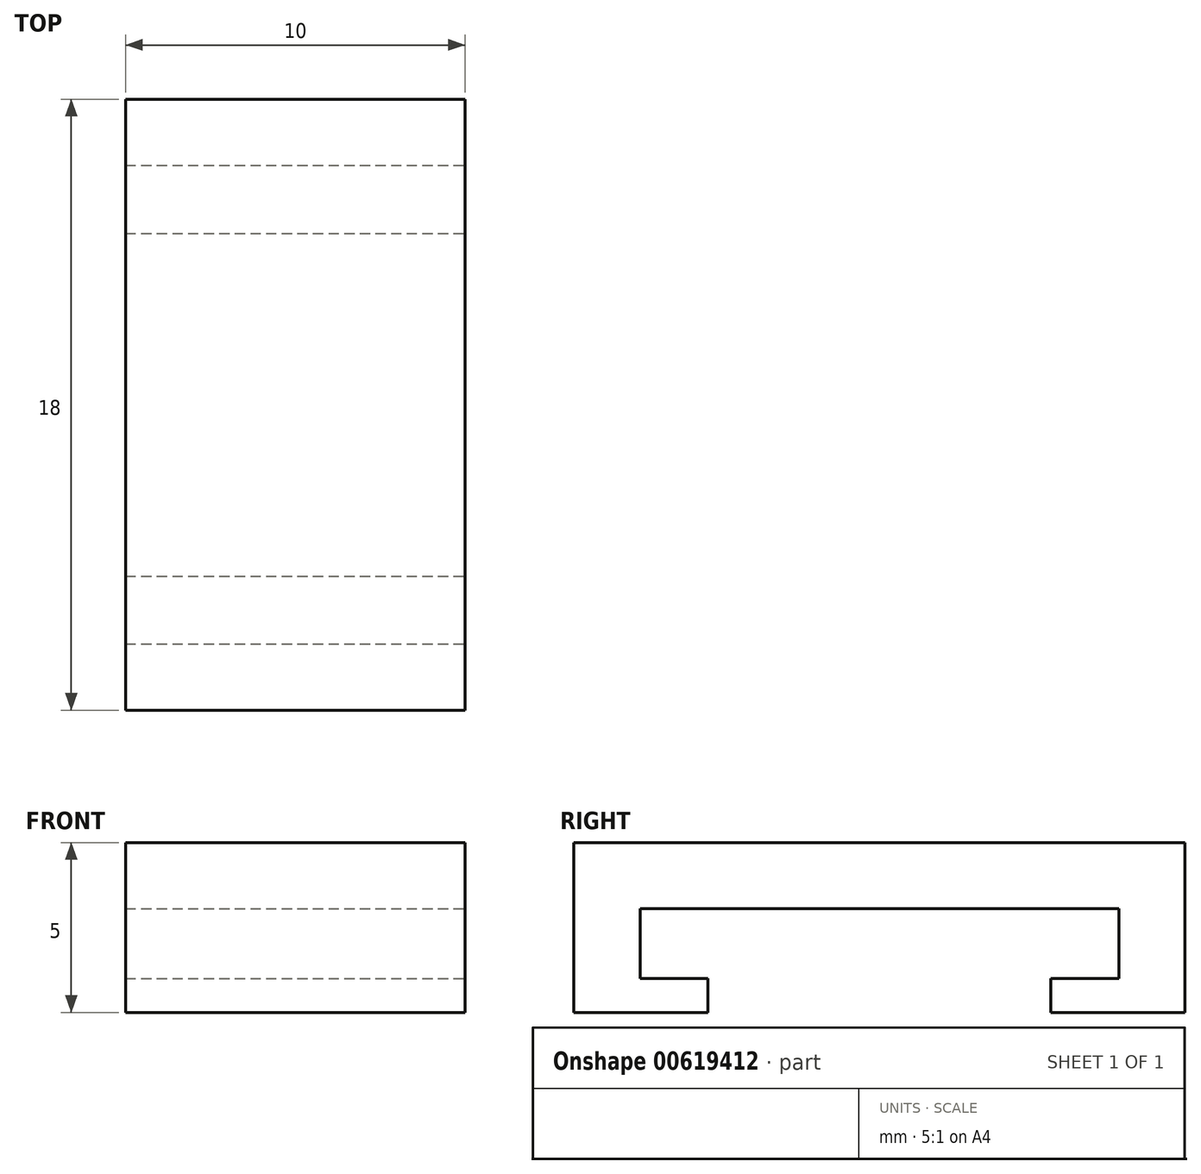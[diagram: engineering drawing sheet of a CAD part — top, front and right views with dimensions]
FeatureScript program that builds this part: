
annotation { "Feature Type Name" : "Feature", "Feature Type Description" : "" }
export const myFeature = defineFeature(function(context is Context, id is Id, definition is map)
    precondition{}
    {
        {
            var Q0;
            Q0=qCreatedBy(makeId("Top.planeOp"),FACE);
            var sketch = newSketch(context, id + "F0", { "sketchPlane" : qUnion([Q0])});
            skLineSegment(sketch, "E0.bottom", {"start": v(-5, 9) * mm, "end": v(5, 9) * mm});
            skLineSegment(sketch, "E0.top", {"start": v(-5, -9) * mm, "end": v(5, -9) * mm});
            skLineSegment(sketch, "E0.left", {"start": v(-5, 9) * mm, "end": v(-5, -9) * mm});
            skLineSegment(sketch, "E0.right", {"start": v(5, 9) * mm, "end": v(5, -9) * mm});
            skPoint(sketch, "E0.middle", {"position": v(0, 0) * mm});
            skSolve(sketch);
        }
        {
            var Q0;
            Q0 = qSketchRegion(id + "F0", true);
            extrude(context, id + "F1", {"entities" : qUnion([Q0]), "depth" : 5 * mm, "offsetDistance" : 25 * mm});
        }
        {
            var Q0;
            Q0=makeQuery(id+"F1.opExtrude","SWEPT_FACE",FACE,{"disambiguationData":[OSD([sQuery(id+"F0.wireOp",EDGE,"E0.right")])]});
            var sketch = newSketch(context, id + "F2", { "sketchPlane" : qUnion([Q0])});
            skLineSegment(sketch, "E1", {"start": v(-5.05, 0) * mm, "end": v(-5.05, 1) * mm});
            skLineSegment(sketch, "E2", {"start": v(-5.05, 1) * mm, "end": v(-7.05, 1) * mm});
            skLineSegment(sketch, "E3", {"start": v(-7.05, 1) * mm, "end": v(-7.05, 3.05) * mm});
            skLineSegment(sketch, "E4", {"start": v(-7.05, 3.05) * mm, "end": v(7.05, 3.05) * mm});
            skLineSegment(sketch, "E5", {"start": v(7.05, 3.05) * mm, "end": v(7.05, 1) * mm});
            skLineSegment(sketch, "E6", {"start": v(7.05, 1) * mm, "end": v(5.05, 1) * mm});
            skLineSegment(sketch, "E7", {"start": v(5.05, 1) * mm, "end": v(5.05, 0) * mm});
            skSolve(sketch);
        }
        {
            var Q0;
            {var subQ0=sQuery(id+"F2.wireOp",EDGE,"E1");Q0=makeQuery(id+"F2.imprint","IMPRINT",FACE,{"disambiguationData":[TD([[makeQuery(id+"F2.imprint","IMPRINT",EDGE,{"derivedFrom":subQ0}),-1.0]])]});}
            extrude(context, id + "F3", {"entities" : qUnion([Q0]), "operationType" : NewBodyOperationType.REMOVE, "endBound" : BoundingType.THROUGH_ALL, "oppositeDirection" : true, "depth" : 25 * mm, "offsetDistance" : 25 * mm});
        }
    });
